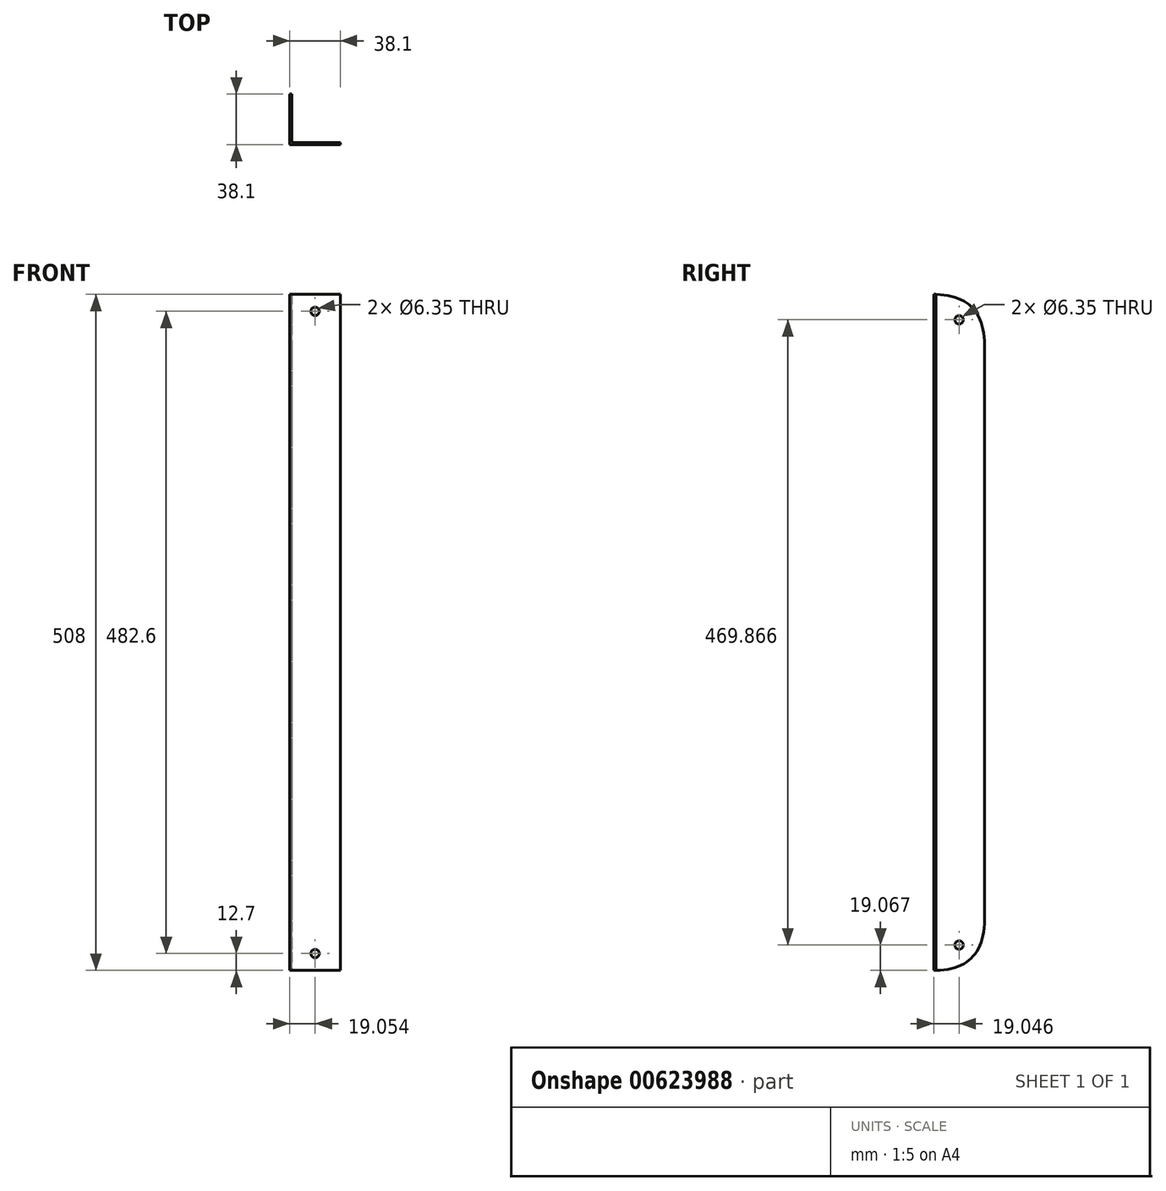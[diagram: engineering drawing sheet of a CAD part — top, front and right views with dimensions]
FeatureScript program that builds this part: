
annotation { "Feature Type Name" : "Feature", "Feature Type Description" : "" }
export const myFeature = defineFeature(function(context is Context, id is Id, definition is map)
    precondition{}
    {
        {
            var Q0;
            Q0=qCreatedBy(makeId("Top.planeOp"),FACE);
            var sketch = newSketch(context, id + "F0", { "sketchPlane" : qUnion([Q0])});
            skLineSegment(sketch, "E0", {"start": v(-12.95, 18.7) * mm, "end": v(-12.95, -19.4) * mm});
            skLineSegment(sketch, "E1", {"start": v(-12.95, -19.4) * mm, "end": v(25.15, -19.4) * mm});
            skLineSegment(sketch, "E2", {"start": v(25.15, -19.4) * mm, "end": v(25.15, -17.8) * mm});
            skLineSegment(sketch, "E3", {"start": v(25.15, -17.8) * mm, "end": v(-11.36, -17.8) * mm});
            skLineSegment(sketch, "E4", {"start": v(-11.36, -17.8) * mm, "end": v(-11.36, 18.7) * mm});
            skLineSegment(sketch, "E5", {"start": v(-11.36, 18.7) * mm, "end": v(-12.95, 18.7) * mm});
            skSolve(sketch);
        }
        {
            var Q0;
            Q0=makeQuery(id+"F0.imprint","IMPRINT",FACE,{"disambiguationData":[TD([[makeQuery(id+"F0.imprint","IMPRINT",EDGE,{"derivedFrom":sQuery(id+"F0.wireOp",EDGE,"E0")}),1.0]])]});
            extrude(context, id + "F1", {"entities" : qUnion([Q0]), "depth" : 508 * mm, "offsetDistance" : 25.4 * mm});
        }
        {
            var Q0;
            Q0=makeQuery(id+"F1.opExtrude","CAP_EDGE",EDGE,{"disambiguationData":[OSD([sQuery(id+"F0.wireOp",EDGE,"E5")])],"isStart":false});
            var Q1;
            Q1=makeQuery(id+"F1.opExtrude","CAP_EDGE",EDGE,{"disambiguationData":[OSD([sQuery(id+"F0.wireOp",EDGE,"E5")])],"isStart":true});
            fillet(context, id + "F2", {"entities" : qUnion([Q0, Q1]), "radius" : 38.1 * mm, "tangentPropagation" : true, "rho" : 0.5, "crossSection" : FilletCrossSection.CONIC, "allowEdgeOverflow" : false});
        }
        {
            var Q0;
            Q0=makeQuery(id+"F1.opExtrude","SWEPT_FACE",FACE,{"disambiguationData":[OSD([sQuery(id+"F0.wireOp",EDGE,"E0")])]});
            var sketch = newSketch(context, id + "F3", { "sketchPlane" : qUnion([Q0])});
            skCircle(sketch, "E6", {"center": v(0.34, 19.07) * mm, "radius": 3.17 * mm});
            skCircle(sketch, "E7", {"center": v(0.34, 488.93) * mm, "radius": 3.18 * mm});
            skSolve(sketch);
        }
        {
            var Q0;
            Q0=makeQuery(id+"F3.imprint","IMPRINT",FACE,{"disambiguationData":[TD([[makeQuery(id+"F3.imprint","IMPRINT",EDGE,{"derivedFrom":sQuery(id+"F3.wireOp",EDGE,"E7")}),1.0]])]});
            var Q1;
            Q1=makeQuery(id+"F3.imprint","IMPRINT",FACE,{"disambiguationData":[TD([[makeQuery(id+"F3.imprint","IMPRINT",EDGE,{"derivedFrom":sQuery(id+"F3.wireOp",EDGE,"E6")}),1.0]])]});
            extrude(context, id + "F4", {"entities" : qUnion([Q0, Q1]), "operationType" : NewBodyOperationType.REMOVE, "oppositeDirection" : true, "depth" : 1.59 * mm, "offsetDistance" : 25.4 * mm});
        }
        {
            var Q0;
            Q0=makeQuery(id+"F1.opExtrude","SWEPT_FACE",FACE,{"disambiguationData":[OSD([sQuery(id+"F0.wireOp",EDGE,"E1")])]});
            var sketch = newSketch(context, id + "F5", { "sketchPlane" : qUnion([Q0])});
            skCircle(sketch, "E8", {"center": v(6.1, 495.3) * mm, "radius": 3.18 * mm});
            skCircle(sketch, "E9", {"center": v(6.1, 12.7) * mm, "radius": 3.18 * mm});
            skSolve(sketch);
        }
        {
            var Q0;
            Q0=makeQuery(id+"F5.imprint","IMPRINT",FACE,{"disambiguationData":[TD([[makeQuery(id+"F5.imprint","IMPRINT",EDGE,{"derivedFrom":sQuery(id+"F5.wireOp",EDGE,"E9")}),1.0]])]});
            var Q1;
            Q1=makeQuery(id+"F5.imprint","IMPRINT",FACE,{"disambiguationData":[TD([[makeQuery(id+"F5.imprint","IMPRINT",EDGE,{"derivedFrom":sQuery(id+"F5.wireOp",EDGE,"E8")}),1.0]])]});
            extrude(context, id + "F6", {"entities" : qUnion([Q0, Q1]), "operationType" : NewBodyOperationType.REMOVE, "oppositeDirection" : true, "depth" : 1.59 * mm, "offsetDistance" : 25.4 * mm});
        }
    });
